annotation { "Feature Type Name" : "Feature", "Feature Type Description" : "" }
export const myFeature = defineFeature(function(context is Context, id is Id, definition is map)
    precondition{}
    {
        {
            var Q0;
            Q0=qCreatedBy(makeId("Front.planeOp"),FACE);
            var sketch = newSketch(context, id + "F0", { "sketchPlane" : qUnion([Q0])});
            skText(sketch, "E0", { "text": "Makerspace Vordingborg.", "fontName": "AllertaStencil-Regular.ttf"});
            skText(sketch, "E1", { "text": "Sebastian Rydiander Larsen\n\n", "fontName": "AllertaStencil-Regular.ttf"});
            skLineSegment(sketch, "E2", {"start": v(-74.92, 26.94) * mm, "end": v(-126.8, 0) * mm});
            skLineSegment(sketch, "E3", {"start": v(-126.8, 0) * mm, "end": v(-74.92, -33.3) * mm});
            skLineSegment(sketch, "E4", {"start": v(-74.92, -33.3) * mm, "end": v(-38.35, -33.3) * mm});
            skLineSegment(sketch, "E5", {"start": v(-38.35, -33.3) * mm, "end": v(0, -75.6) * mm});
            skLineSegment(sketch, "E6", {"start": v(-74.92, 26.94) * mm, "end": v(0, 26.94) * mm});
            skLineSegment(sketch, "E7", {"start": v(0, 26.94) * mm, "end": v(0, -75.6) * mm});
            skLineSegment(sketch, "E8.MirrorCS", {"start": v(74.92, 26.94) * mm, "end": v(0, 26.94) * mm});
            skLineSegment(sketch, "E9.MirrorCS", {"start": v(74.92, 26.94) * mm, "end": v(126.8, 0) * mm});
            skLineSegment(sketch, "E10.MirrorCS", {"start": v(126.8, 0) * mm, "end": v(74.92, -33.3) * mm});
            skLineSegment(sketch, "E11.MirrorCS", {"start": v(74.92, -33.3) * mm, "end": v(38.35, -33.3) * mm});
            skLineSegment(sketch, "E12.MirrorCS", {"start": v(38.35, -33.3) * mm, "end": v(0, -75.6) * mm});
            skCircle(sketch, "E13", {"center": v(0, 20.67) * mm, "radius": 1.5 * mm});
            const initialGuessF0  = {"E0": [-0.0711, 0.00543, 1, 0, 0.00903], "E1": [-0.07064, -0.02032, 1, 0, 0.0078]};
            skSetInitialGuess(sketch, initialGuessF0);
            skSolve(sketch);
        }
        {
            var Q0;
            Q0=makeQuery(id+"F0.imprint","IMPRINT",FACE,{"disambiguationData":[TD([[makeQuery(id+"F0.imprint","IMPRINT",EDGE,{"derivedFrom":sQuery(id+"F0.wireOp",EDGE,"E0.sketch_text.stroke-0")}),1.0]])]});
            var Q1;
            Q1=makeQuery(id+"F0.imprint","IMPRINT",FACE,{"disambiguationData":[TD([[makeQuery(id+"F0.imprint","IMPRINT",EDGE,{"derivedFrom":sQuery(id+"F0.wireOp",EDGE,"E0.sketch_text.stroke-203")}),1.0]])]});
            var Q2;
            Q2=makeQuery(id+"F0.imprint","IMPRINT",FACE,{"disambiguationData":[TD([[makeQuery(id+"F0.imprint","IMPRINT",EDGE,{"derivedFrom":sQuery(id+"F0.wireOp",EDGE,"E0.sketch_text.stroke-290")}),1.0]])]});
            extrude(context, id + "F1", {"entities" : qUnion([Q0, Q1, Q2]), "depth" : 4 * mm});
        }
    });